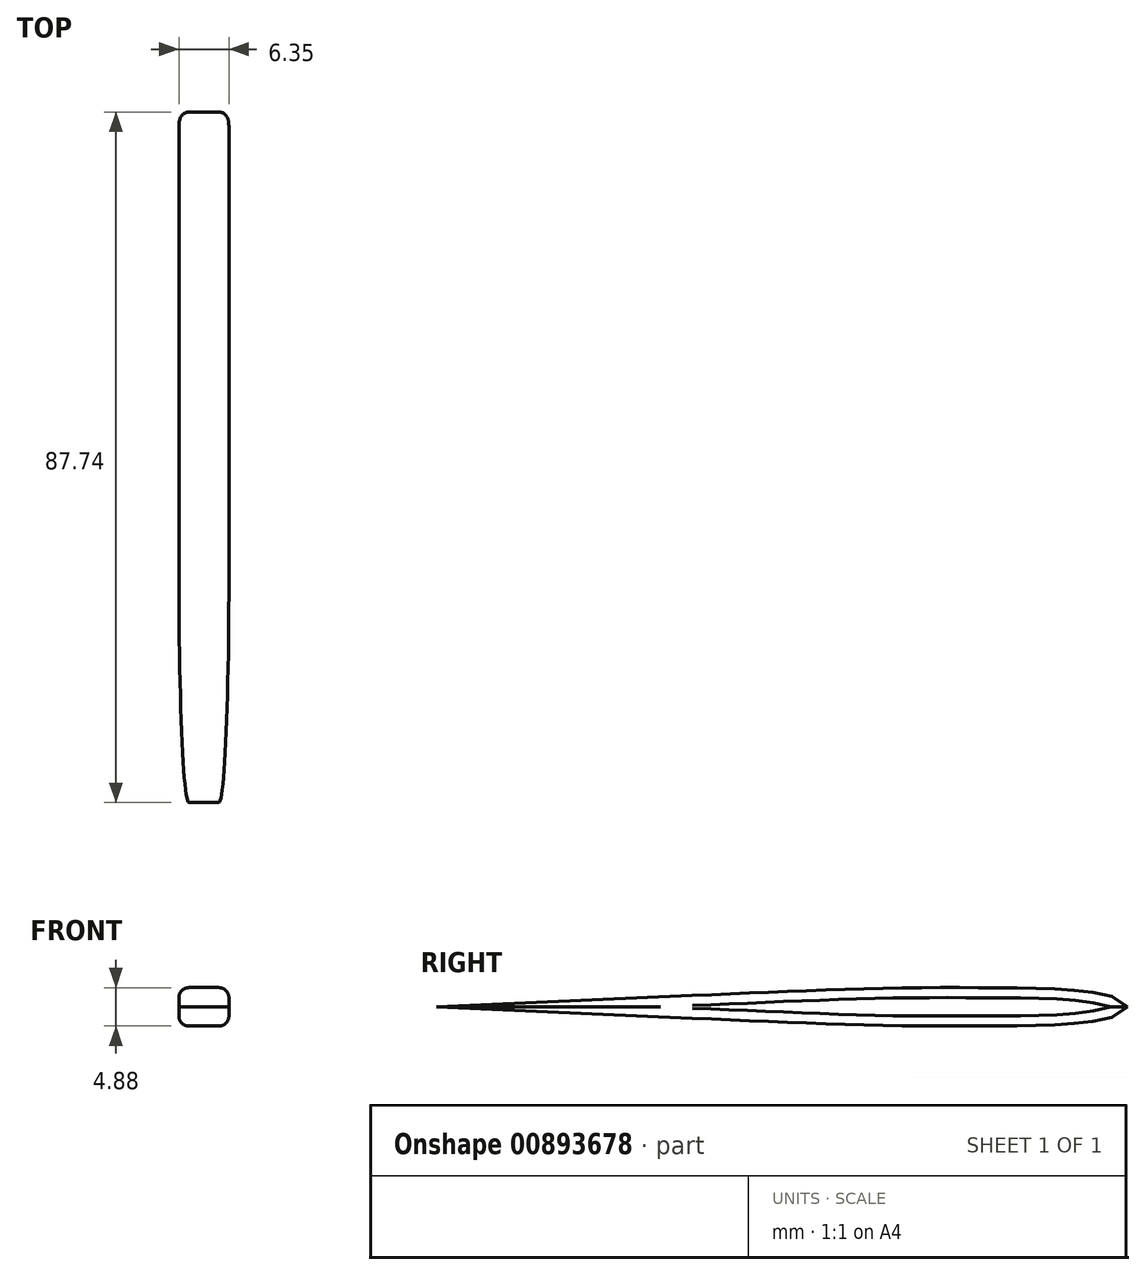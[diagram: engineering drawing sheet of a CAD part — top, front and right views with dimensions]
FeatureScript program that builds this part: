
annotation { "Feature Type Name" : "Feature", "Feature Type Description" : "" }
export const myFeature = defineFeature(function(context is Context, id is Id, definition is map)
    precondition{}
    {
        {
            var Q0;
            Q0=qCreatedBy(makeId("Right.planeOp"),FACE);
            var sketch = newSketch(context, id + "F0", { "sketchPlane" : qUnion([Q0])});
            skFitSpline(sketch, "E0", {"points": [v(47.12, 0) * mm, v(46.6, -0.62) * mm, v(45.32, -1.26) * mm, v(44.45, -1.52) * mm, v(43.56, -1.68) * mm, v(42.05, -1.92) * mm, v(39.13, -2.22) * mm, v(34.15, -2.39) * mm, v(21.26, -2.43) * mm, v(10.75, -2.22) * mm, v(-8.15, -1.45) * mm], "startDerivative": vector(-9.38, -14.32) * mm, "endDerivative": vector(-96.51, 3.93) * mm});
            skLineSegment(sketch, "E1", {"start": v(-8.15, -1.45) * mm, "end": v(-40.62, 0) * mm});
            skLineSegment(sketch, "E2.MirrorCS", {"start": v(-8.15, 1.45) * mm, "end": v(-40.62, 0) * mm});
            skFitSpline(sketch, "E3.MirrorCS", {"points": [v(47.12, 0) * mm, v(46.6, 0.62) * mm, v(45.32, 1.26) * mm, v(44.45, 1.52) * mm, v(43.56, 1.68) * mm, v(42.05, 1.92) * mm, v(39.13, 2.22) * mm, v(34.15, 2.39) * mm, v(21.26, 2.43) * mm, v(10.75, 2.22) * mm, v(-8.15, 1.45) * mm], "startDerivative": vector(-9.38, 14.32) * mm, "endDerivative": vector(-96.51, -3.93) * mm});
            skSolve(sketch);
        }
        {
            var Q0;
            Q0=makeQuery(id+"F0.imprint","IMPRINT",FACE,{"disambiguationData":[TD([[makeQuery(id+"F0.imprint","IMPRINT",EDGE,{"derivedFrom":sQuery(id+"F0.wireOp",EDGE,"E0")}),-1.0]])]});
            extrude(context, id + "F1", {"entities" : qUnion([Q0]), "depth" : 6.35 * mm, "offsetDistance" : 25.4 * mm});
        }
        {
            var Q0;
            Q0=makeQuery(id+"F1.opExtrude","CAP_EDGE",EDGE,{"disambiguationData":[OSD([sQuery(id+"F0.wireOp",EDGE,"E0")])],"isStart":true});
            var Q1;
            Q1=makeQuery(id+"F1.opExtrude","CAP_EDGE",EDGE,{"disambiguationData":[OSD([sQuery(id+"F0.wireOp",EDGE,"E0")])],"isStart":false});
            var Q2;
            Q2=makeQuery(id+"F1.opExtrude","CAP_EDGE",EDGE,{"disambiguationData":[OSD([sQuery(id+"F0.wireOp",EDGE,"E3.MirrorCS")])],"isStart":true});
            var Q3;
            Q3=makeQuery(id+"F1.opExtrude","CAP_EDGE",EDGE,{"disambiguationData":[OSD([sQuery(id+"F0.wireOp",EDGE,"E3.MirrorCS")])],"isStart":false});
            var Q4;
            Q4=makeQuery(id+"F1.opExtrude","CAP_EDGE",EDGE,{"disambiguationData":[OSD([sQuery(id+"F0.wireOp",EDGE,"E1")])],"isStart":false});
            var Q5;
            Q5=makeQuery(id+"F1.opExtrude","CAP_EDGE",EDGE,{"disambiguationData":[OSD([sQuery(id+"F0.wireOp",EDGE,"E2.MirrorCS")])],"isStart":false});
            var Q6;
            Q6=makeQuery(id+"F1.opExtrude","CAP_EDGE",EDGE,{"disambiguationData":[OSD([sQuery(id+"F0.wireOp",EDGE,"E1")])],"isStart":true});
            var Q7;
            Q7=makeQuery(id+"F1.opExtrude","CAP_EDGE",EDGE,{"disambiguationData":[OSD([sQuery(id+"F0.wireOp",EDGE,"E2.MirrorCS")])],"isStart":true});
            fillet(context, id + "F2", {"entities" : qUnion([Q0, Q1, Q2, Q3, Q4, Q5, Q6, Q7]), "radius" : 1.27 * mm, "tangentPropagation" : true, "allowEdgeOverflow" : false});
        }
    });
